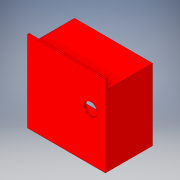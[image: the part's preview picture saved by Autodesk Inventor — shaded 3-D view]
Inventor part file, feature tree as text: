
AUTODESK INVENTOR PART (.ipt)
format: ipt  version: 2018 (Build 220112000, 112)  size: 241,152 bytes
history: native  units: in
note: dims shown in document units (in); Inventor stores cm internally (conversion verified against a paired STEP export)
features: sketch x11, extrude x10, shell x2, fillet x1
ambient origin geometry x8: Origin, YZ Plane, XZ Plane, XY Plane, X Axis, Y Axis, Z Axis, Center Point
bodies: Solid1 (feature_tree)
feature tree (24):
  extrude  "Extrusion1"  Depth=6.0in
  shell  "Shell1"  Thickness=6.0in
  extrude  "Extrusion6"  Depth=0.25in TaperAngle=0.0deg
  extrude  "Extrusion10"  Depth=1.1in
  extrude  "Extrusion11"  Depth=0.25in
  fillet  "Fillet1"  Radius=0.25in
  extrude  "Extrusion12"  Depth=0.125in
  shell  "Shell2"  Thickness=0.125in
  extrude  "Extrusion13"  Depth=0.125in
  sketch  "Sketch14"  dims[d69=6.0in d70=5.5in]
  extrude  "Extrusion18"  Depth=5.5in
  extrude  "Extrusion19"  Depth=0.25in
  extrude  "Extrusion22"  Depth=0.25in TaperAngle=0.0deg
  extrude  "Extrusion23"  Depth=1.25in
  sketch  "Sketch1"  dims[d0=6.0in d1=6.0in d2=6.0in d3=0.0in]
  sketch  "Sketch6"  dims[d4=0.25in d36=0.25in d37=0.0in]
  sketch  "Sketch10"  dims[d55=1.1in d56=1.1in]
  sketch  "Sketch11"  dims[d57=1.1in d58=1.1in d59=0.25in d60=0.0in]
  sketch  "Sketch12"  dims[d61=0.2in d62=0.125in d63=0.125in]
  sketch  "Sketch13"  dims[d64=1.8125in d65=5.0in d66=0.0in d67=0.0in d68=0.125in]
  sketch  "Sketch22"  dims[d71=3.5in d72=0.0in d73=0.25in]
  sketch  "Sketch23"  dims[d75=2.0in d76=0.0in d100=0.25in d101=0.0in]
  sketch  "Sketch27"  dims[d120=1.15in d121=1.25in]
  sketch  "Sketch28"  dims[d122=1.15in d123=1.25in d128=1.15in d129=1.25in d130=0.5in d131=0.5in d132=0.775in d133=0.6in d134=0.6in d135=0.6in d136=2.0in d142=1.5in d143=1.5in d144=1.15in d145=2.0in d147=1.15in d148=1.25in d149=2.425in d150=1.15in d151=1.25in d152=1.25in d153=0.25in d154=0.0in d169=0.1in d170=0.1in d171=0.11in d172=0.11in d173=0.3in d174=0.0in d176=1.0in d177=3.625in d178=0.0in]
